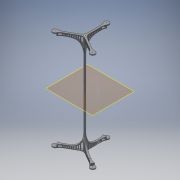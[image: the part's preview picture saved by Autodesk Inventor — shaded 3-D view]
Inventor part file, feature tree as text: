
AUTODESK INVENTOR PART (.ipt)
format: ipt  version: 2018 (Build 220112000, 112)  size: 1,348,608 bytes
history: native  units: in
note: dims shown in document units (in); Inventor stores cm internally (conversion verified against a paired STEP export)
features: sketch x12, extrude x8, revolve x2, mirror x2, fillet x1, plane x1, projected_geometry x1
ambient origin geometry x8: Origin, YZ Plane, XZ Plane, XY Plane, X Axis, Y Axis, Z Axis, Center Point
bodies: Solid1 (feature_tree)
feature tree (27):
  extrude  "Extrusion1"  Depth=78.7402in
  revolve  "Revolution1"  [1 undecoded]
  extrude  "Extrusion2"  Depth=98.4252in
  extrude  "Extrusion3"  TaperAngle=90.0deg  [1 undecoded]
  sketch  "Sketch7"  dims[d63=393.7008in d67=90.0deg d68=30.0deg]
  fillet  "Fillet2"  [1 undecoded]
  revolve  "Revolution2"  [1 undecoded]
  mirror  "Mirror3"
  extrude  "Extrusion4"  Depth=236.2205in
  sketch  "Sketch11"  dims[d79=196.8504in d82=393.7008in]
  plane  "Work Plane2"
  mirror  "Mirror4"
  extrude  "Extrusion5"  Depth=393.7008in
  extrude  "Extrusion6"  Depth=2435.3204in TaperAngle=0.0deg
  extrude  "Extrusion7"  Depth=98.4252in
  extrude  "Extrusion8"  Depth=19.685in
  sketch  "Sketch1"  dims[d0=78.7402in d1=88.5827in]
  sketch  "Sketch2"  dims[d2=5905.5118in d3=0.0in]
  sketch  "Sketch3"  dims[d17=3.9201in d18=3.9465in d45=19.6875in d47=19.685in d56=19.685in d60=39.3701in]
  sketch  "Sketch5"  dims[d61=196.8504in d62=98.4252in]
  sketch  "Sketch9"  dims[d69=150.0deg d70=236.2205in]
  sketch  "Sketch10"  dims[d76=3937.0079in d77=0.0in d78=236.2205in]
  sketch  "Sketch12"  dims[d83=393.7008in d84=2435.3204in d85=0.0in]
  sketch  "Sketch13"  dims[d87=393.7008in d90=98.4252in d91=393.7008in]
  sketch  "Sketch14"  dims[d92=90.0deg d93=19.685in]
  sketch  "Sketch15"  dims[d94=3.5433in d96=78.7402in d97=0.3937in d99=0.3937in d101=1.1811in d103=360.0deg d105=2435.3204in d106=0.0in d107=19.685in d108=19.685in d109=19.685in d110=2435.3204in d111=0.0in d112=137.7953in d113=39.3701in d114=0.0in d115=1.1811in d117=360.0deg d119=78.7402in d120=0.0in d121=157.4803in d122=0.0in]
  projected_geometry  "Projected Loop2"
note: 4 required parameter values undecoded (feature->parameter linkage not recoverable at this tier; creation-order binding heuristic only, values carry confidence <= 0.55)